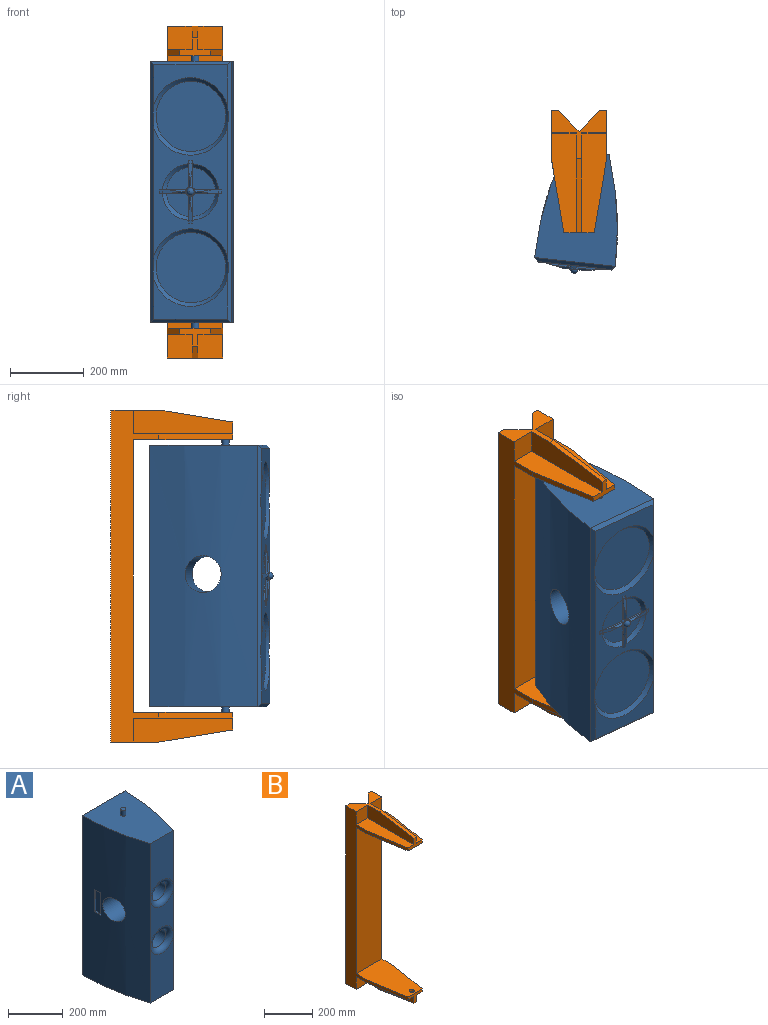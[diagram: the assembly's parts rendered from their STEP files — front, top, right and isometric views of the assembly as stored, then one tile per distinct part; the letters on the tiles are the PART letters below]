
ASSEMBLY  parts=2 mates=1
PART A: 61 faces, bbox 220.1x330.1x760.1 mm
  f0: cylinder r=925mm len=710mm, axis (0,0,1), area 208956.8mm2, adj f3,f4,f5,f15,f55
  f1: cylinder r=925mm len=710mm, axis (0,0,1), area 205951mm2, adj f3,f4,f5,f14,f55,f56,f57,f58
  f2: plane 345.97x200mm, normal (0,1,0), area 28988mm2, adj f11,f14,f15,f16,f17,f28,f30,f31
  f3: plane 710x120mm, normal (0,-1,0), area 63990.4mm2, adj f0,f1,f4,f5,f22,f23
  f4: plane 300x220mm, normal (0,0,-1), area 55796.5mm2, adj f0,f1,f3,f12,f26
  f5: plane 300x220mm, normal (0,0,1), area 55796.5mm2, adj f0,f1,f3,f13,f24
  f6: plane 200x107.98mm, normal (0,1,0), area 10896.4mm2, adj f11,f12,f14,f15
  f7: plane 200x107.98mm, normal (0,1,0), area 10896.4mm2, adj f13,f14,f15,f16
  f8: plane 190x190mm, normal (0,1,0), area 28352.9mm2, adj f11
  f9: plane 133.35x133.35mm, normal (0,1,0), area 13966.1mm2, adj f17
  f10: plane 190x190mm, normal (0,1,0), area 28352.9mm2, adj f16
  f11: cone r=95mm half-angle=45deg, axis (0,1,0), area 8581mm2, adj f2,f6,f8,f14,f15
  f12: plane 220x10mm, normal (0,0.71,-0.71), area 2969.8mm2, adj f4,f6,f14,f15
  f13: plane 220x10mm, normal (0,0.71,0.71), area 2969.8mm2, adj f5,f7,f14,f15
  f14: plane 710x10.03mm, normal (-0.71,0.71,0), area 9597.7mm2, adj f1,f2,f6,f7,f11,f12,f13,f16
  f15: plane 710x10mm, normal (0.71,0.71,0), area 9597.6mm2, adj f0,f2,f6,f7,f11,f12,f13,f16
  f16: cone r=95mm half-angle=45deg, axis (0,1,0), area 8581mm2, adj f2,f7,f10,f14,f15
  f17: cone r=66.67mm half-angle=45deg, axis (0,1,0), area 6368.9mm2, adj f2,f9,f41
  f18: cylinder r=38.1mm len=230mm, axis (0,-1,0), area 55059.6mm2, adj f19,f22
  f19: plane 76.2x76.2mm, normal (0,-1,0), area 4560.4mm2, adj f18
  f20: cylinder r=38.1mm len=230mm, axis (0,-1,0), area 55059.6mm2, adj f21,f23
  f21: plane 76.2x76.2mm, normal (0,-1,0), area 4560.4mm2, adj f20
  f22: torus R=58.1mm, axis (0,-1,0), area 8955.2mm2, adj f3,f18
  f23: torus R=58.1mm, axis (0,-1,0), area 8955.2mm2, adj f3,f20
  f24: cylinder r=10mm len=25mm, axis (0,0,-1), area 1570.8mm2, adj f5,f25
  f25: plane 20x20mm, normal (0,0,1), area 314.2mm2, adj f24
  f26: cylinder r=10mm len=25mm, axis (0,0,1), area 1570.8mm2, adj f4,f27
  f27: plane 20x20mm, normal (0,0,-1), area 314.2mm2, adj f26
  f28: plane 73.54x5mm, normal (0,0,1), area 296.8mm2, adj f2,f29,f41,f45,f52
  f29: cylinder r=12.5mm len=12.5mm, axis (0,-1,0), area 119.2mm2, adj f28,f30,f40,f41,f50,f52
  f30: plane 73.54x5mm, normal (-1,0,0), area 296.8mm2, adj f2,f29,f41,f42,f50
  f31: plane 73.54x5mm, normal (1,0,0), area 296.8mm2, adj f2,f32,f41,f42,f51
  f32: cylinder r=12.5mm len=12.5mm, axis (0,-1,0), area 119.2mm2, adj f31,f33,f40,f41,f48,f51
  f33: plane 73.54x5mm, normal (0,0,1), area 296.8mm2, adj f2,f32,f41,f43,f48
  f34: plane 73.54x5mm, normal (0,0,-1), area 296.8mm2, adj f2,f35,f41,f43,f49
  f35: cylinder r=12.5mm len=12.5mm, axis (0,-1,0), area 119.2mm2, adj f34,f36,f40,f41,f46,f49
  f36: plane 73.54x5mm, normal (1,0,0), area 296.8mm2, adj f2,f35,f41,f44,f46
  f37: plane 73.54x5mm, normal (-1,0,0), area 296.8mm2, adj f2,f38,f41,f44,f47
  f38: cylinder r=12.5mm len=12.5mm, axis (0,-1,0), area 119.2mm2, adj f37,f39,f40,f41,f47,f53
  f39: plane 73.54x5mm, normal (0,0,-1), area 296.8mm2, adj f2,f38,f41,f45,f53
  f40: plane 25x25mm, normal (0,1,0), area 176.7mm2, adj f29,f32,f35,f38,f54
  f41: plane 153.35x153.35mm, normal (0,-1,0), area 3069.3mm2, adj f17,f28,f29,f30,f31,f32,f33,f34
  f42: plane 56.71x10mm, normal (0,0.98,0.17), area 431.9mm2, adj f2,f30,f31,f50,f51
  f43: plane 56.71x10mm, normal (0.17,0.98,0), area 431.9mm2, adj f2,f33,f34,f48,f49
  f44: plane 56.71x10mm, normal (0,0.98,-0.17), area 431.9mm2, adj f2,f36,f37,f46,f47
  f45: plane 56.71x10mm, normal (-0.17,0.98,0), area 431.9mm2, adj f2,f28,f39,f52,f53
  f46: plane 45.3x5.11mm, normal (0.71,0.71,0), area 214.3mm2, adj f35,f36,f44,f47
  f47: plane 45.3x5.11mm, normal (-0.71,0.71,0), area 214.3mm2, adj f37,f38,f44,f46
  f48: plane 45.3x5.11mm, normal (0,0.71,0.71), area 214.3mm2, adj f32,f33,f43,f49
  f49: plane 45.3x5.11mm, normal (0,0.71,-0.71), area 214.3mm2, adj f34,f35,f43,f48
  f50: plane 45.3x5.11mm, normal (-0.71,0.71,0), area 214.3mm2, adj f29,f30,f42,f51
  f51: plane 45.3x5.11mm, normal (0.71,0.71,0), area 214.3mm2, adj f31,f32,f42,f50
  f52: plane 45.3x5.11mm, normal (0,0.71,0.71), area 214.3mm2, adj f28,f29,f45,f53
  f53: plane 45.3x5.11mm, normal (0,0.71,-0.71), area 214.3mm2, adj f38,f39,f45,f52
  f54: sphere r=10mm, area 628.3mm2, adj f40
  f55: cylinder r=50mm len=209.16mm, axis (-1,0,0), area 60982.2mm2, adj f0,f1
  f56: plane 30x8.05mm, normal (0,0,1), area 207.4mm2, adj f1,f57,f59,f60
  f57: plane 100x8.05mm, normal (0,-1,0), area 805.2mm2, adj f1,f56,f58,f60
  f58: plane 30x8.05mm, normal (0,0,-1), area 207.4mm2, adj f1,f57,f59,f60
  f59: plane 100x5.61mm, normal (0,1,0), area 561.1mm2, adj f1,f56,f58,f60
  f60: plane 100x30mm, normal (-1,0,0), area 3000mm2, adj f56,f57,f58,f59
PART B: 35 faces, bbox 150x330x900 mm
  f0: plane 900x130mm, normal (-1,0,0), area 56100mm2, adj f3,f7,f9,f10,f12,f13,f14,f17
  f1: plane 900x130mm, normal (1,0,0), area 56100mm2, adj f3,f4,f6,f7,f9,f11,f13,f14
  f2: plane 82.5x47.5mm, normal (0,-1,0), area 1725mm2, adj f3,f4,f18,f19,f20,f24,f25,f26
  f3: plane 270x150mm, normal (0,0,1), area 33435.8mm2, adj f0,f1,f2,f9,f24,f25,f29
  f4: plane 270x67.5mm, normal (0,0,-1), area 14850mm2, adj f1,f2,f15,f20,f24
  f5: plane 82.5x47.5mm, normal (0,-1,0), area 1725mm2, adj f6,f7,f8,f16,f17,f21,f22,f23
  f6: plane 270x67.5mm, normal (0,0,1), area 14850mm2, adj f1,f5,f11,f16,f22
  f7: plane 270x150mm, normal (0,0,-1), area 33435.8mm2, adj f0,f1,f5,f9,f22,f23,f27
  f8: plane 270x65mm, normal (-1,0,0), area 14300mm2, adj f5,f12,f14,f17,f21
  f9: plane 740x150mm, normal (0,-1,0), area 111000mm2, adj f0,f1,f3,f7
  f10: plane 67.5x65mm, normal (0,-1,0), area 4387.5mm2, adj f0,f13,f18,f19
  f11: plane 67.5x65mm, normal (0,-1,0), area 4387.5mm2, adj f1,f6,f14,f16
  f12: plane 67.5x65mm, normal (0,-1,0), area 4387.5mm2, adj f0,f8,f14,f17
  f13: plane 150x130mm, normal (0,0,-1), area 7025mm2, adj f0,f1,f10,f15,f19,f20,f26,f31
  f14: plane 150x130mm, normal (0,0,1), area 7025mm2, adj f0,f1,f8,f11,f12,f16,f21,f31
  f15: plane 67.5x65mm, normal (0,-1,0), area 4387.5mm2, adj f1,f4,f13,f20
  f16: plane 270x65mm, normal (1,0,0), area 14300mm2, adj f5,f6,f11,f14,f21
  f17: plane 270x67.5mm, normal (0,0,1), area 14850mm2, adj f0,f5,f8,f12,f23
  f18: plane 270x67.5mm, normal (0,0,-1), area 14850mm2, adj f0,f2,f10,f19,f25
  f19: plane 270x65mm, normal (-1,0,0), area 14300mm2, adj f2,f10,f13,f18,f26
  f20: plane 270x65mm, normal (1,0,0), area 14300mm2, adj f2,f4,f13,f15,f26
  f21: plane 200x32.5mm, normal (0,-0.16,0.99), area 3039.4mm2, adj f5,f8,f14,f16
  f22: plane 200x33.75mm, normal (0.99,-0.17,0), area 3042.4mm2, adj f1,f5,f6,f7
  f23: plane 200x33.75mm, normal (-0.99,-0.17,0), area 3042.4mm2, adj f0,f5,f7,f17
  f24: plane 200x33.75mm, normal (0.99,-0.17,0), area 3042.4mm2, adj f1,f2,f3,f4
  f25: plane 200x33.75mm, normal (-0.99,-0.17,0), area 3042.4mm2, adj f0,f2,f3,f18
  f26: plane 200x32.5mm, normal (0,-0.16,-0.99), area 3039.4mm2, adj f2,f13,f19,f20
  f27: cylinder r=10mm len=20mm, axis (0,0,-1), area 628.3mm2, adj f7,f28
  f28: plane 20x20mm, normal (0,0,-1), area 314.2mm2, adj f27
  f29: cylinder r=10mm len=20mm, axis (0,0,1), area 628.3mm2, adj f3,f30
  f30: plane 20x20mm, normal (0,0,1), area 314.2mm2, adj f29
  f31: plane 900x20mm, normal (0,1,0), area 18000mm2, adj f1,f13,f14,f33
  f32: plane 900x20mm, normal (0,1,0), area 18000mm2, adj f0,f13,f14,f34
  f33: plane 900x55mm, normal (-0.71,0.71,0), area 70003.6mm2, adj f13,f14,f31,f34
  f34: plane 900x55mm, normal (0.71,0.71,0), area 70003.6mm2, adj f13,f14,f32,f33
PLACE A rot(axis=(0,0,1),173.7deg) t=(400,-594.96,-103.81)mm
PLACE B t=(226.62,-153.5,-8.81)mm fixed
MATE revolute A.f24 <-> B.f27  axis (0,0,1) through (301.62,-483.5,-78.81)mm
